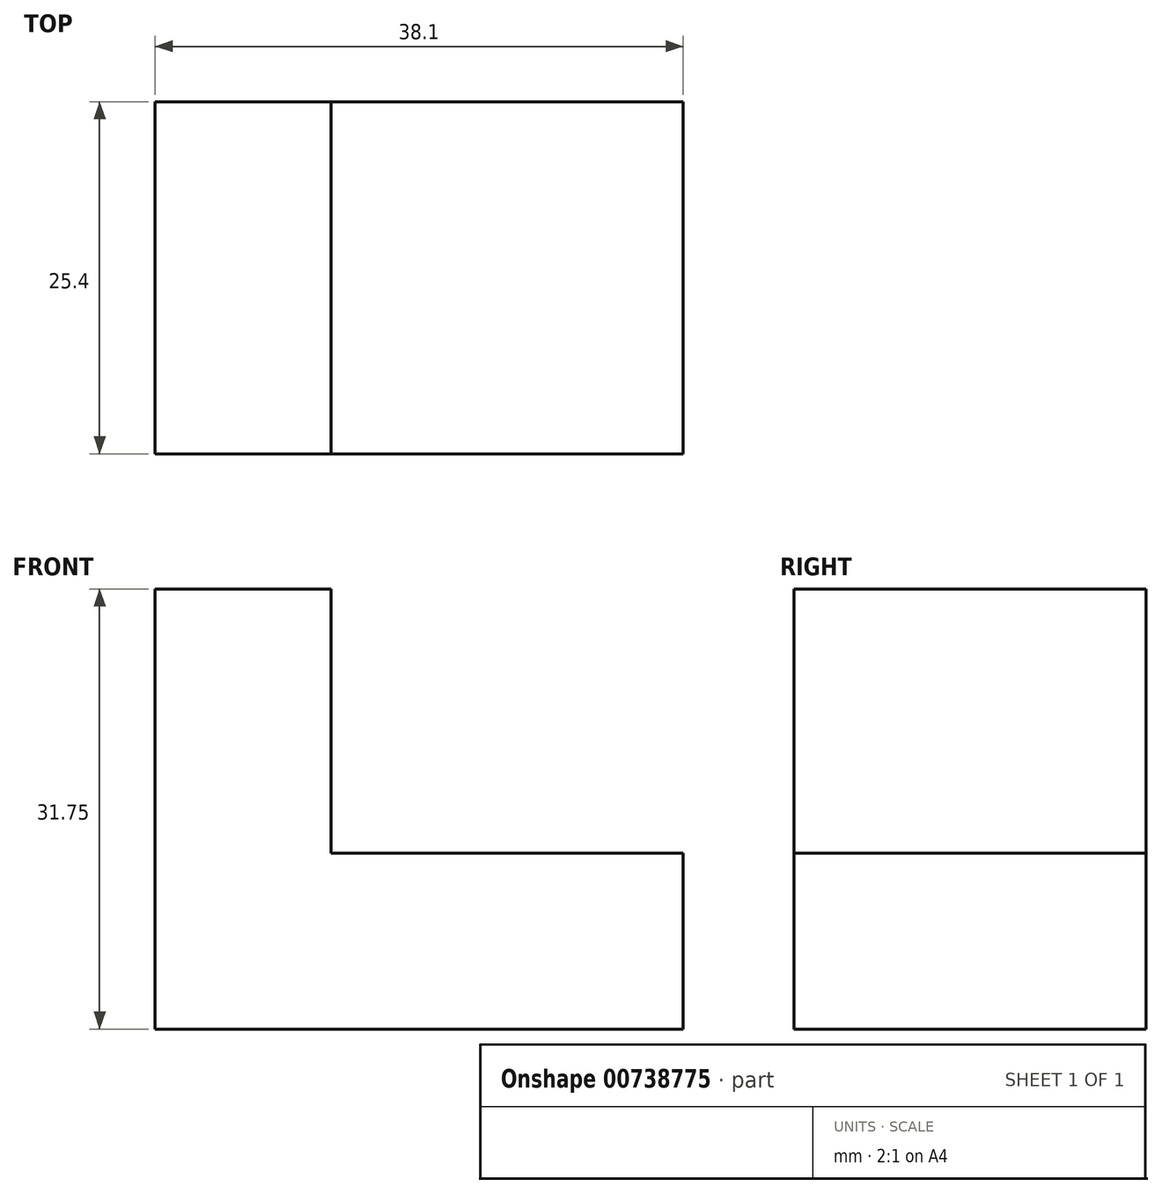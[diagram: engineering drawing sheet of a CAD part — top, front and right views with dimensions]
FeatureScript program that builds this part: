
annotation { "Feature Type Name" : "Feature", "Feature Type Description" : "" }
export const myFeature = defineFeature(function(context is Context, id is Id, definition is map)
    precondition{}
    {
        {
            var Q0;
            Q0=qCreatedBy(makeId("Front.planeOp"),FACE);
            var sketch = newSketch(context, id + "F0", { "sketchPlane" : qUnion([Q0])});
            skLineSegment(sketch, "E0", {"start": v(0, 31.75) * mm, "end": v(12.7, 31.75) * mm});
            skLineSegment(sketch, "E1", {"start": v(12.7, 31.75) * mm, "end": v(12.7, 12.7) * mm});
            skLineSegment(sketch, "E2", {"start": v(12.7, 12.7) * mm, "end": v(38.1, 12.7) * mm});
            skLineSegment(sketch, "E3", {"start": v(38.1, 12.7) * mm, "end": v(38.1, 0) * mm});
            skLineSegment(sketch, "E4", {"start": v(38.1, 0) * mm, "end": v(0, 0) * mm});
            skLineSegment(sketch, "E5", {"start": v(0, 0) * mm, "end": v(0, 31.75) * mm});
            skSolve(sketch);
        }
        {
            var Q0;
            Q0 = qSketchRegion(id + "F0", true);
            extrude(context, id + "F1", {"entities" : qUnion([Q0]), "depth" : 25.4 * mm, "offsetDistance" : 25.4 * mm});
        }
    });
